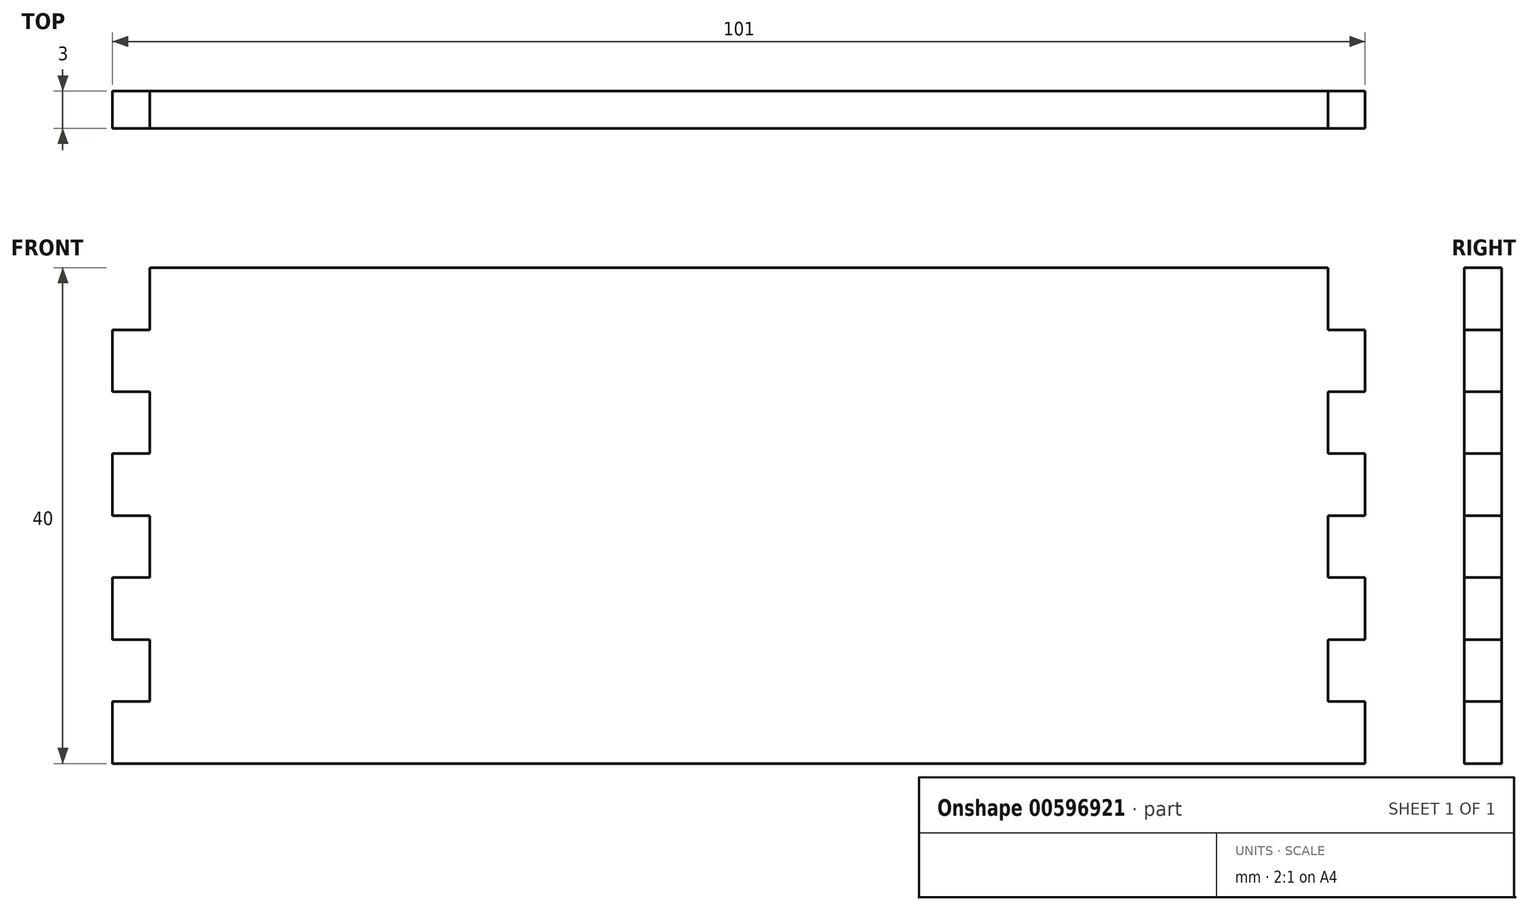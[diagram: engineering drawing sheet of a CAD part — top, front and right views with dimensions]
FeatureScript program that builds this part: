
annotation { "Feature Type Name" : "Feature", "Feature Type Description" : "" }
export const myFeature = defineFeature(function(context is Context, id is Id, definition is map)
    precondition{}
    {
        {
            var Q0;
            Q0=qCreatedBy(makeId("Front.planeOp"),FACE);
            var sketch = newSketch(context, id + "F0", { "sketchPlane" : qUnion([Q0])});
            skLineSegment(sketch, "E0.bottom", {"start": v(47.5, 20) * mm, "end": v(-47.5, 20) * mm});
            skLineSegment(sketch, "E0.top", {"start": v(47.5, -20) * mm, "end": v(-47.5, -20) * mm});
            skLineSegment(sketch, "E0.left", {"start": v(47.5, 20) * mm, "end": v(47.5, -20) * mm});
            skLineSegment(sketch, "E0.right", {"start": v(-47.5, 20) * mm, "end": v(-47.5, -20) * mm});
            skPoint(sketch, "E0.middle", {"position": v(0, 0) * mm});
            skSolve(sketch);
        }
        {
            var Q0;
            Q0 = qSketchRegion(id + "Fv06wUQ1Qcaubfx_0", true);
            var Q1;
            Q1 = qSketchRegion(id + "F0", true);
            extrude(context, id + "F1", {"entities" : qUnion([Q0, Q1]), "depth" : 3 * mm, "offsetDistance" : 25 * mm});
        }
        {
            var Q0;
            Q0=makeQuery(id+"F1.opExtrude","CAP_FACE",FACE,{"disambiguationData":[OSD([sQuery(id+"F0.wireOp",EDGE,"E0.bottom"),sQuery(id+"F0.wireOp",EDGE,"E0.top"),sQuery(id+"F0.wireOp",EDGE,"E0.left"),sQuery(id+"F0.wireOp",EDGE,"E0.right")])],"isStart":false});
            var sketch = newSketch(context, id + "F2", { "sketchPlane" : qUnion([Q0])});
            skLineSegment(sketch, "E1.bottom", {"start": v(-47.5, -20) * mm, "end": v(-50.5, -20) * mm});
            skLineSegment(sketch, "E1.top", {"start": v(-47.5, -15) * mm, "end": v(-50.5, -15) * mm});
            skLineSegment(sketch, "E1.left", {"start": v(-47.5, -20) * mm, "end": v(-47.5, -15) * mm});
            skLineSegment(sketch, "E1.right", {"start": v(-50.5, -20) * mm, "end": v(-50.5, -15) * mm});
            skLineSegment(sketch, "E2.0.1.0", {"start": v(-47.5, -5) * mm, "end": v(-50.5, -5) * mm});
            skLineSegment(sketch, "E2.0.1.1", {"start": v(-50.5, -10) * mm, "end": v(-50.5, -5) * mm});
            skLineSegment(sketch, "E2.0.1.2", {"start": v(-47.5, -10) * mm, "end": v(-47.5, -5) * mm});
            skLineSegment(sketch, "E2.0.1.3", {"start": v(-47.5, -10) * mm, "end": v(-50.5, -10) * mm});
            skLineSegment(sketch, "E2.0.2.0", {"start": v(-47.5, 5) * mm, "end": v(-50.5, 5) * mm});
            skLineSegment(sketch, "E2.0.2.1", {"start": v(-50.5, 0) * mm, "end": v(-50.5, 5) * mm});
            skLineSegment(sketch, "E2.0.2.2", {"start": v(-47.5, 0) * mm, "end": v(-47.5, 5) * mm});
            skLineSegment(sketch, "E2.0.2.3", {"start": v(-47.5, 0) * mm, "end": v(-50.5, 0) * mm});
            skLineSegment(sketch, "E2.0.3.0", {"start": v(-47.5, 15) * mm, "end": v(-50.5, 15) * mm});
            skLineSegment(sketch, "E2.0.3.1", {"start": v(-50.5, 10) * mm, "end": v(-50.5, 15) * mm});
            skLineSegment(sketch, "E2.0.3.2", {"start": v(-47.5, 10) * mm, "end": v(-47.5, 15) * mm});
            skLineSegment(sketch, "E2.0.3.3", {"start": v(-47.5, 10) * mm, "end": v(-50.5, 10) * mm});
            skLineSegment(sketch, "E2.direction1", {"start": v(-50.5, -15) * mm, "end": v(-26, -15) * mm, "construction": true});
            skLineSegment(sketch, "E2.direction2", {"start": v(-50.5, -15) * mm, "end": v(-50.5, -5) * mm, "construction": true});
            skLineSegment(sketch, "E3.MirrorCS", {"start": v(47.5, -5) * mm, "end": v(50.5, -5) * mm});
            skLineSegment(sketch, "E4.MirrorCS", {"start": v(47.5, -15) * mm, "end": v(50.5, -15) * mm});
            skLineSegment(sketch, "E5.MirrorCS", {"start": v(47.5, -20) * mm, "end": v(50.5, -20) * mm});
            skLineSegment(sketch, "E6.MirrorCS", {"start": v(47.5, 10) * mm, "end": v(50.5, 10) * mm});
            skLineSegment(sketch, "E7.MirrorCS", {"start": v(47.5, 15) * mm, "end": v(50.5, 15) * mm});
            skLineSegment(sketch, "E8.MirrorCS", {"start": v(47.5, 0) * mm, "end": v(50.5, 0) * mm});
            skLineSegment(sketch, "E9.MirrorCS", {"start": v(47.5, 5) * mm, "end": v(50.5, 5) * mm});
            skLineSegment(sketch, "E10.MirrorCS", {"start": v(47.5, -10) * mm, "end": v(50.5, -10) * mm});
            skLineSegment(sketch, "E11.MirrorCS", {"start": v(50.5, -10) * mm, "end": v(50.5, -5) * mm});
            skLineSegment(sketch, "E12.MirrorCS", {"start": v(47.5, -10) * mm, "end": v(47.5, -5) * mm});
            skLineSegment(sketch, "E13.MirrorCS", {"start": v(50.5, -20) * mm, "end": v(50.5, -15) * mm});
            skLineSegment(sketch, "E14.MirrorCS", {"start": v(47.5, -20) * mm, "end": v(47.5, -15) * mm});
            skLineSegment(sketch, "E15.MirrorCS", {"start": v(47.5, 10) * mm, "end": v(47.5, 15) * mm});
            skLineSegment(sketch, "E16.MirrorCS", {"start": v(50.5, 10) * mm, "end": v(50.5, 15) * mm});
            skLineSegment(sketch, "E17.MirrorCS", {"start": v(50.5, -15) * mm, "end": v(50.5, -5) * mm, "construction": true});
            skLineSegment(sketch, "E18.MirrorCS", {"start": v(47.5, 0) * mm, "end": v(47.5, 5) * mm});
            skLineSegment(sketch, "E19.MirrorCS", {"start": v(50.5, 0) * mm, "end": v(50.5, 5) * mm});
            skSolve(sketch);
        }
        {
            var Q0;
            Q0 = qSketchRegion(id + "F2", true);
            extrude(context, id + "F3", {"entities" : qUnion([Q0]), "operationType" : NewBodyOperationType.ADD, "oppositeDirection" : true, "depth" : 3 * mm, "offsetDistance" : 25 * mm});
        }
    });
